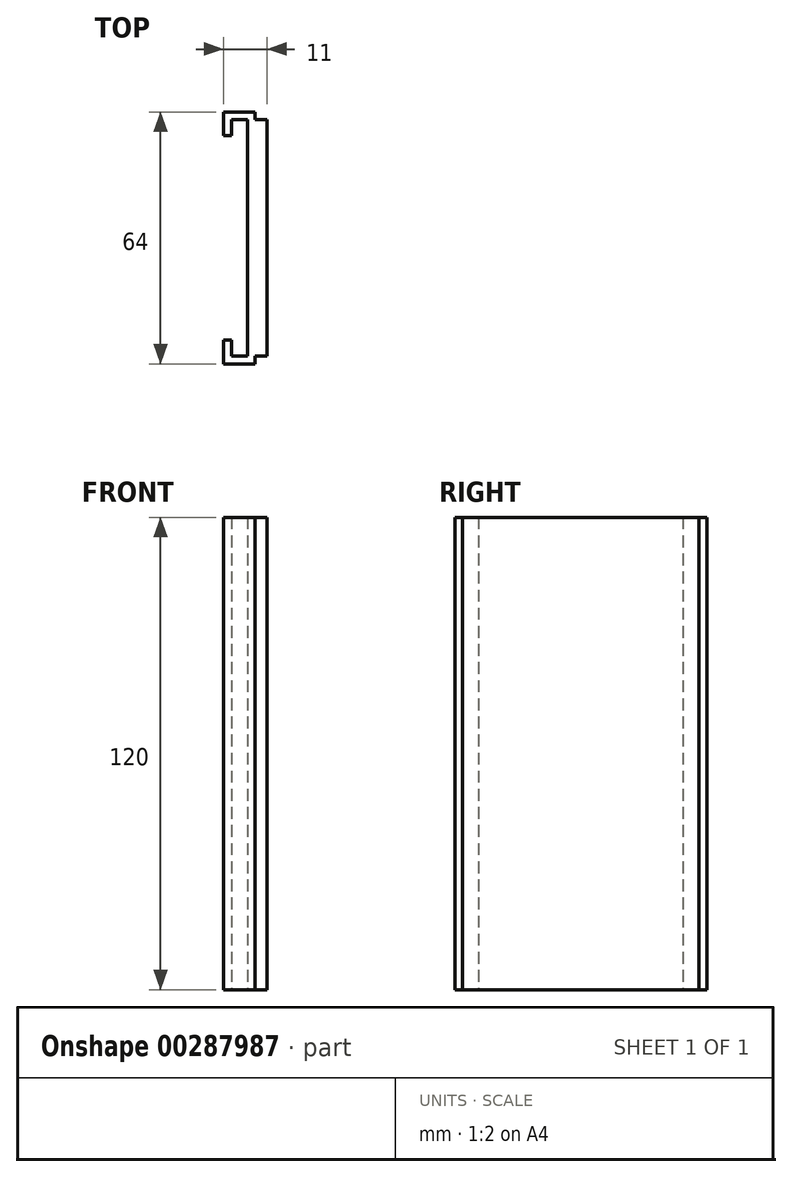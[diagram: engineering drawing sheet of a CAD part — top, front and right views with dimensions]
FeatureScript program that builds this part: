
annotation { "Feature Type Name" : "Feature", "Feature Type Description" : "" }
export const myFeature = defineFeature(function(context is Context, id is Id, definition is map)
    precondition{}
    {
        {
            var Q0;
            Q0=qCreatedBy(makeId("Top.planeOp"),FACE);
            var sketch = newSketch(context, id + "F0", { "sketchPlane" : qUnion([Q0])});
            skLineSegment(sketch, "E0.left", {"start": v(-5, 30) * mm, "end": v(-5, -30) * mm});
            skPoint(sketch, "E0.middle", {"position": v(0, 0) * mm});
            skLineSegment(sketch, "E1.MirrorCS", {"start": v(-5, -30) * mm, "end": v(-5, 30) * mm});
            skLineSegment(sketch, "E2.left", {"start": v(-5, 23.5) * mm, "end": v(-5, -23.5) * mm});
            skPoint(sketch, "E3", {"position": v(-3, 30) * mm});
            skLineSegment(sketch, "E4.bottom", {"start": v(-3, 30) * mm, "end": v(-11, 30) * mm});
            skLineSegment(sketch, "E4.top", {"start": v(-3, 32) * mm, "end": v(-11, 32) * mm});
            skLineSegment(sketch, "E4.left", {"start": v(-3, 30) * mm, "end": v(-3, 32) * mm});
            skLineSegment(sketch, "E4.right", {"start": v(-11, 30) * mm, "end": v(-11, 32) * mm});
            skLineSegment(sketch, "E5.bottom", {"start": v(-11, 32) * mm, "end": v(-9, 32) * mm});
            skLineSegment(sketch, "E5.top", {"start": v(-11, 26) * mm, "end": v(-9, 26) * mm});
            skLineSegment(sketch, "E5.left", {"start": v(-11, 32) * mm, "end": v(-11, 26) * mm});
            skLineSegment(sketch, "E5.right", {"start": v(-9, 32) * mm, "end": v(-9, 26) * mm});
            skLineSegment(sketch, "E6.MirrorCS", {"start": v(-11, -32) * mm, "end": v(-9, -32) * mm});
            skLineSegment(sketch, "E7.MirrorCS", {"start": v(-3, -30) * mm, "end": v(-3, -32) * mm});
            skLineSegment(sketch, "E8.MirrorCS", {"start": v(-11, -30) * mm, "end": v(-11, -32) * mm});
            skLineSegment(sketch, "E9.MirrorCS", {"start": v(-3, -30) * mm, "end": v(-11, -30) * mm});
            skPoint(sketch, "E10.MirrorP", {"position": v(-3, -30) * mm});
            skLineSegment(sketch, "E11.MirrorCS", {"start": v(-3, -32) * mm, "end": v(-11, -32) * mm});
            skLineSegment(sketch, "E12.MirrorCS", {"start": v(-11, -26) * mm, "end": v(-9, -26) * mm});
            skLineSegment(sketch, "E13.MirrorCS", {"start": v(-9, -32) * mm, "end": v(-9, -26) * mm});
            skLineSegment(sketch, "E14.MirrorCS", {"start": v(-11, -32) * mm, "end": v(-11, -26) * mm});
            skLineSegment(sketch, "E15.left", {"start": v(0, 30) * mm, "end": v(0, -30) * mm});
            skLineSegment(sketch, "E16.bottom", {"start": v(-5, 30) * mm, "end": v(0, 30) * mm});
            skLineSegment(sketch, "E16.top", {"start": v(-5, -30) * mm, "end": v(0, -30) * mm});
            skSolve(sketch);
        }
        {
            var Q0;
            Q0 = qSketchRegion(id + "F0", true);
            extrude(context, id + "F1", {"entities" : qUnion([Q0]), "depth" : 60 * mm, "hasSecondDirection" : true, "secondDirectionOppositeDirection" : true, "secondDirectionDepth" : 60 * mm});
        }
    });
